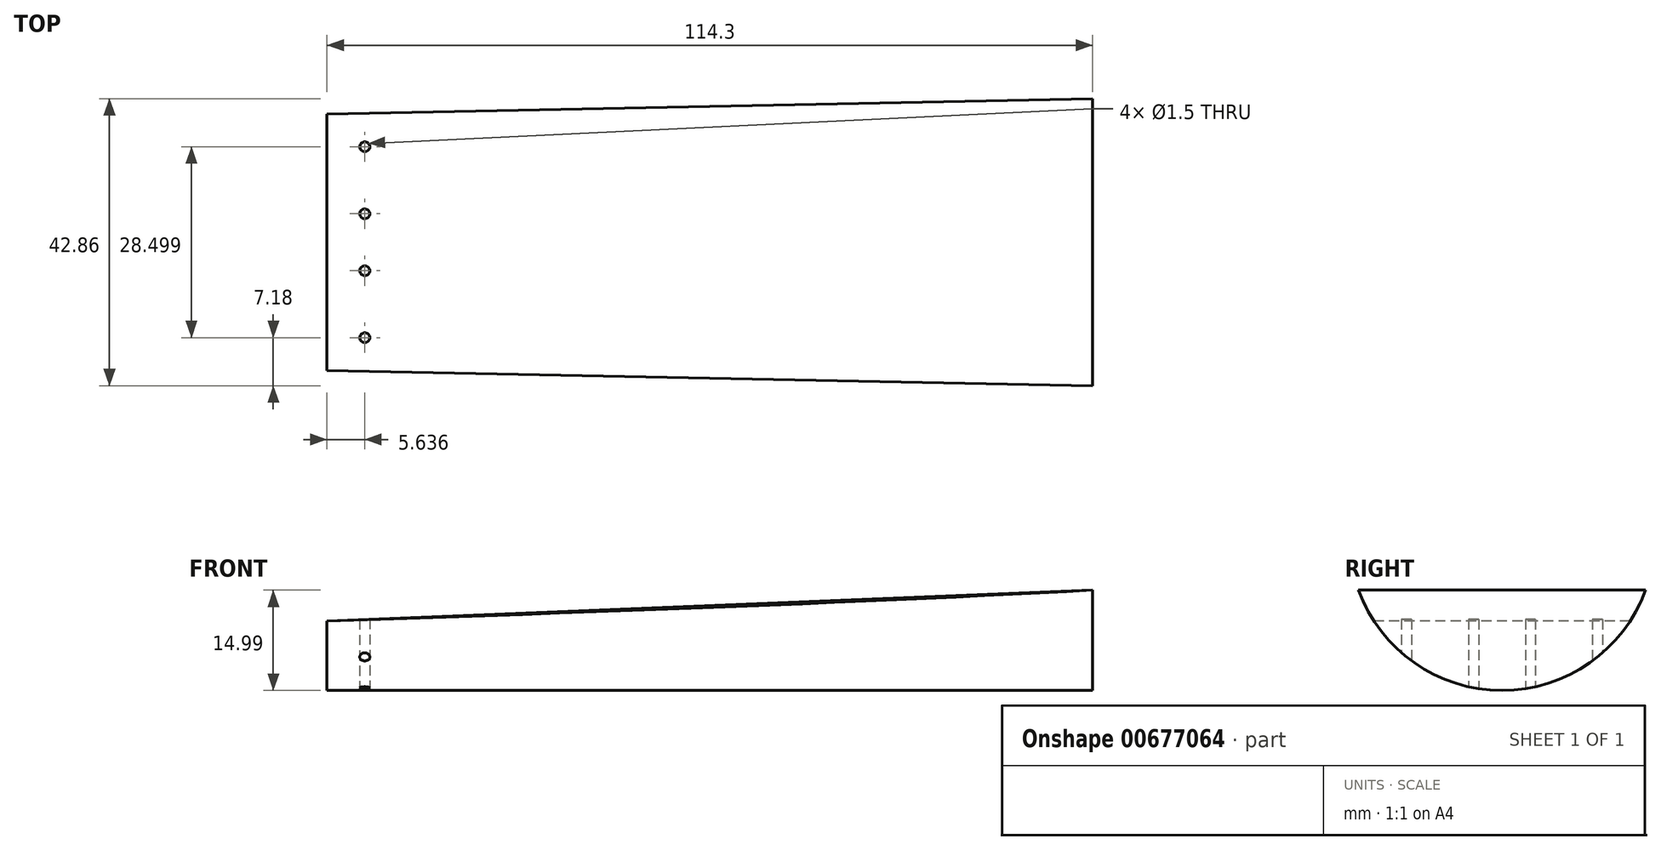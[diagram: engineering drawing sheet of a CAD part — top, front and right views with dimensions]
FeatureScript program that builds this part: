
annotation { "Feature Type Name" : "Feature", "Feature Type Description" : "" }
export const myFeature = defineFeature(function(context is Context, id is Id, definition is map)
    precondition{}
    {
        {
            var Q0;
            Q0=qCreatedBy(makeId("Top.planeOp"),FACE);
            var sketch = newSketch(context, id + "F0", { "sketchPlane" : qUnion([Q0])});
            skLineSegment(sketch, "E0", {"start": v(-59.33, 19.05) * mm, "end": v(-59.33, -19.05) * mm});
            skLineSegment(sketch, "E1", {"start": v(-59.33, -19.05) * mm, "end": v(59.33, -21.43) * mm});
            skLineSegment(sketch, "E2", {"start": v(59.33, -21.43) * mm, "end": v(59.33, 21.43) * mm});
            skLineSegment(sketch, "E3", {"start": v(59.33, 21.43) * mm, "end": v(-59.33, 19.05) * mm});
            skPoint(sketch, "E4.endSnap0", {"position": v(0, -20.24) * mm});
            skLineSegment(sketch, "E5", {"start": v(-59.33, 0) * mm, "end": v(59.33, 0) * mm, "construction": true});
            skLineSegment(sketch, "E6", {"start": v(0, 20.24) * mm, "end": v(0, -20.24) * mm, "construction": true});
            skCircle(sketch, "E7", {"center": v(-49.33, 14.25) * mm, "radius": 0.75 * mm});
            skCircle(sketch, "E8", {"center": v(-49.33, 4.25) * mm, "radius": 0.75 * mm});
            skCircle(sketch, "E9.MirrorC", {"center": v(-49.33, -4.25) * mm, "radius": 0.75 * mm});
            skCircle(sketch, "E10.MirrorC", {"center": v(-49.33, -14.25) * mm, "radius": 0.75 * mm});
            skSolve(sketch);
        }
        {
            var Q0;
            Q0 = qSketchRegion(id + "F0", true);
            extrude(context, id + "F1", {"entities" : qUnion([Q0]), "depth" : 15 * mm, "offsetDistance" : 25.4 * mm});
        }
        {
            var Q0;
            Q0=makeQuery(id+"F1.opExtrude","SWEPT_FACE",FACE,{"disambiguationData":[OSD([sQuery(id+"F0.wireOp",EDGE,"E2")])]});
            var sketch = newSketch(context, id + "F2", { "sketchPlane" : qUnion([Q0])});
            skArc(sketch, "E11", {"start": v(-21.43, 14.99) * mm, "mid": v(0, 0) * mm, "end": v(21.43, 14.99) * mm});
            skSolve(sketch);
        }
        {
            var Q0;
            {var subQ1=sQuery(id+"F0.wireOp",EDGE,"E2");var subQ2=makeQuery(id+"F1.opExtrude","CAP_EDGE",EDGE,{"disambiguationData":[OSD([subQ1])],"isStart":false});Q0=makeQuery(id+"F2.imprint","IMPRINT",FACE,{"disambiguationData":[TD([[makeQuery(id+"F2.imprint","IMPRINT",EDGE,{"derivedFrom":subQ2}),-1.0]])]});}
            var Q1;
            {var subQ1=sQuery(id+"F0.wireOp",EDGE,"E0");var subQ2=makeQuery(id+"F1.opExtrude","CAP_EDGE",EDGE,{"disambiguationData":[OSD([subQ1])],"isStart":false});Q1=makeQuery(id+"F7aeL5ArJs9rHA6_1.imprint","IMPRINT",FACE,{"disambiguationData":[TD([[makeQuery(id+"F7aeL5ArJs9rHA6_1.imprint","IMPRINT",EDGE,{"derivedFrom":subQ2}),-1.0]])]});}
            extrude(context, id + "F3", {"entities" : qUnion([Q0, Q1]), "operationType" : NewBodyOperationType.INTERSECT, "oppositeDirection" : true, "depth" : 114.3 * mm, "offsetDistance" : 25.4 * mm});
        }
        {
            var Q0;
            Q0=qCreatedBy(makeId("Front.planeOp"),FACE);
            var sketch = newSketch(context, id + "F4", { "sketchPlane" : qUnion([Q0])});
            skLineSegment(sketch, "E12", {"start": v(-54.97, 10.4) * mm, "end": v(-54.97, 14.99) * mm});
            skLineSegment(sketch, "E13", {"start": v(-54.97, 14.99) * mm, "end": v(59.33, 14.99) * mm});
            skLineSegment(sketch, "E14", {"start": v(59.33, 14.99) * mm, "end": v(-54.97, 10.4) * mm});
            skSolve(sketch);
        }
        {
            var Q0;
            Q0 = qSketchRegion(id + "F4", true);
            extrude(context, id + "F5", {"entities" : qUnion([Q0]), "operationType" : NewBodyOperationType.REMOVE, "oppositeDirection" : true, "depth" : 25.4 * mm, "offsetDistance" : 25.4 * mm, "hasSecondDirection" : true, "secondDirectionOppositeDirection" : false, "secondDirectionDepth" : 25.4 * mm});
        }
    });
